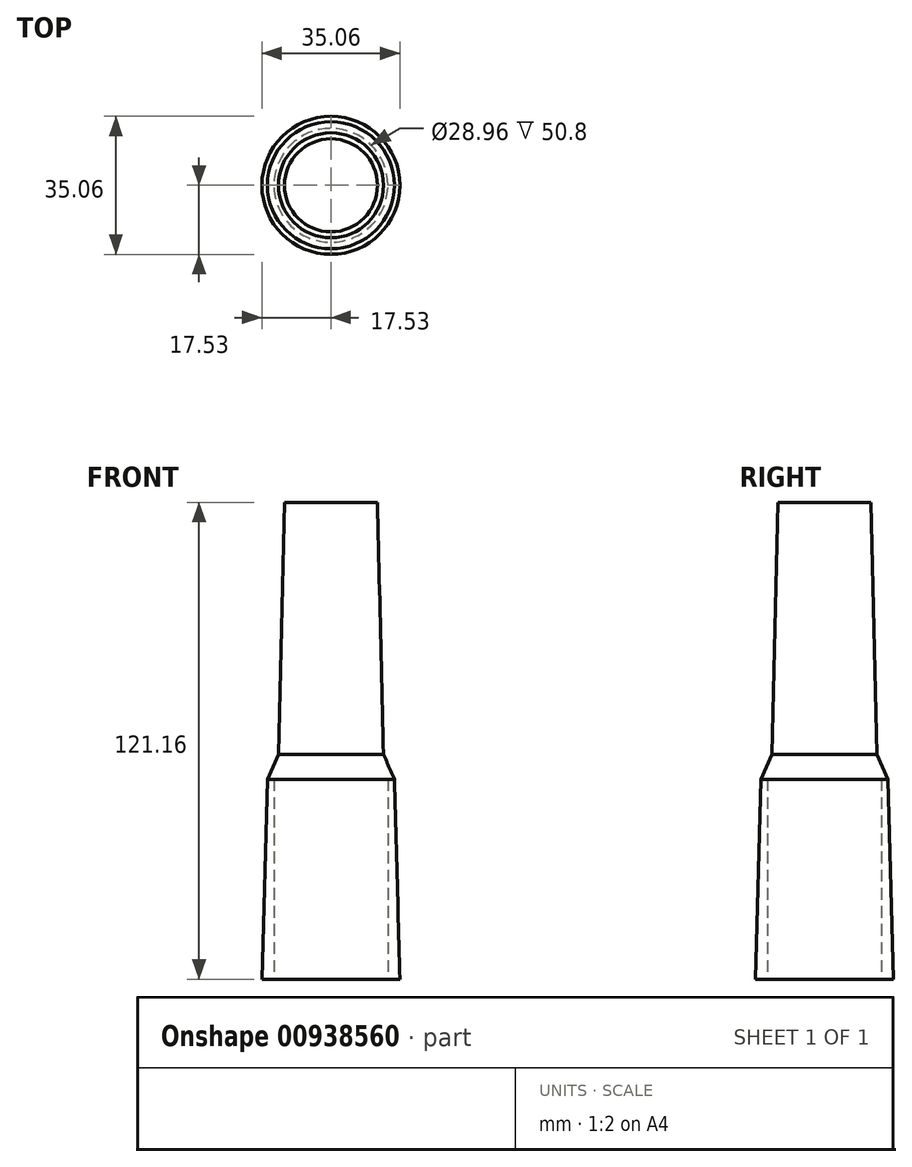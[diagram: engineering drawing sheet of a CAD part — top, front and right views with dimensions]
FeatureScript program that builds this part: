
annotation { "Feature Type Name" : "Feature", "Feature Type Description" : "" }
export const myFeature = defineFeature(function(context is Context, id is Id, definition is map)
    precondition{}
    {
        {
            var Q0;
            Q0=qCreatedBy(makeId("Top.planeOp"),FACE);
            var sketch = newSketch(context, id + "F0", { "sketchPlane" : qUnion([Q0])});
            skCircle(sketch, "E0", {"center": v(0, 0) * mm, "radius": 17.53 * mm});
            skSolve(sketch);
        }
        {
            var Q0;
            Q0=qCreatedBy(makeId("Top.planeOp"),FACE);
            cPlane(context, id + "F1", {"entities" : qUnion([Q0]), "cplaneType" : CPlaneType.OFFSET, "offset" : 50.8 * mm, "width" : 152.4 * mm, "height" : 152.4 * mm});
        }
        {
            var Q0;
            Q0=qCreatedBy(id+"F1.planeOp",FACE);
            var sketch = newSketch(context, id + "F2", { "sketchPlane" : qUnion([Q0])});
            skCircle(sketch, "E1", {"center": v(0, 0) * mm, "radius": 16.13 * mm});
            skSolve(sketch);
        }
        {
            var Q0;
            Q0=makeQuery(id+"F0.imprint","IMPRINT",FACE,{"disambiguationData":[TD([[makeQuery(id+"F0.imprint","IMPRINT",EDGE,{"derivedFrom":sQuery(id+"F0.wireOp",EDGE,"E0")}),1.0]])]});
            var Q1;
            Q1=makeQuery(id+"F2.imprint","IMPRINT",FACE,{"disambiguationData":[TD([[makeQuery(id+"F2.imprint","IMPRINT",EDGE,{"derivedFrom":sQuery(id+"F2.wireOp",EDGE,"E1")}),1.0]])]});
            loft(context, id + "F3", {"sheetProfilesArray" : [{ "sheetProfileEntities" : qUnion([Q0]) }, { "sheetProfileEntities" : qUnion([Q1]) }]});
        }
        {
            var Q0;
            Q0=qCreatedBy(id+"F1.planeOp",FACE);
            cPlane(context, id + "F4", {"entities" : qUnion([Q0]), "cplaneType" : CPlaneType.OFFSET, "offset" : 6.35 * mm, "width" : 152.4 * mm, "height" : 152.4 * mm});
        }
        {
            var Q0;
            Q0=qCreatedBy(id+"F4.planeOp",FACE);
            var sketch = newSketch(context, id + "F5", { "sketchPlane" : qUnion([Q0])});
            skCircle(sketch, "E2", {"center": v(0, 0) * mm, "radius": 13.34 * mm});
            skSolve(sketch);
        }
        {
            var Q1;
            Q1=makeQuery(id+"F3.opLoft","CAP_FACE",FACE,{"disambiguationData":[OSD([makeQuery(id+"F2.imprint","IMPRINT",FACE,{"disambiguationData":[TD([[makeQuery(id+"F2.imprint","IMPRINT",EDGE,{"derivedFrom":sQuery(id+"F2.wireOp",EDGE,"E1")}),1.0]])]})])],"isStart":true});
            var Q2;
            Q2=makeQuery(id+"F5.imprint","IMPRINT",FACE,{"disambiguationData":[TD([[makeQuery(id+"F5.imprint","IMPRINT",EDGE,{"derivedFrom":sQuery(id+"F5.wireOp",EDGE,"E2")}),1.0]])]});
            loft(context, id + "F6", {"operationType" : NewBodyOperationType.ADD, "sheetProfilesArray" : [{ "sheetProfileEntities" : qUnion([Q1]) }, { "sheetProfileEntities" : qUnion([Q2]) }]});
        }
        {
            var Q0;
            Q0=qCreatedBy(id+"F4.planeOp",FACE);
            cPlane(context, id + "F7", {"entities" : qUnion([Q0]), "cplaneType" : CPlaneType.OFFSET, "offset" : 64 * mm, "width" : 152.4 * mm, "height" : 152.4 * mm});
        }
        {
            var Q0;
            Q0=qCreatedBy(id+"F7.planeOp",FACE);
            var sketch = newSketch(context, id + "F8", { "sketchPlane" : qUnion([Q0])});
            skCircle(sketch, "E3", {"center": v(0, 0) * mm, "radius": 11.81 * mm});
            skSolve(sketch);
        }
        {
            var Q1;
            Q1=makeQuery(id+"F6.opLoft","CAP_FACE",FACE,{"disambiguationData":[OSD([makeQuery(id+"F5.imprint","IMPRINT",FACE,{"disambiguationData":[TD([[makeQuery(id+"F5.imprint","IMPRINT",EDGE,{"derivedFrom":sQuery(id+"F5.wireOp",EDGE,"E2")}),1.0]])]})])],"isStart":true});
            var Q2;
            Q2=makeQuery(id+"F8.imprint","IMPRINT",FACE,{"disambiguationData":[TD([[makeQuery(id+"F8.imprint","IMPRINT",EDGE,{"derivedFrom":sQuery(id+"F8.wireOp",EDGE,"E3")}),1.0]])]});
            loft(context, id + "F9", {"operationType" : NewBodyOperationType.ADD, "sheetProfilesArray" : [{ "sheetProfileEntities" : qUnion([Q1]) }, { "sheetProfileEntities" : qUnion([Q2]) }]});
        }
        {
            var Q0;
            Q0=makeQuery(id+"F3.opLoft","CAP_FACE",FACE,{"disambiguationData":[OSD([makeQuery(id+"F0.imprint","IMPRINT",FACE,{"disambiguationData":[TD([[makeQuery(id+"F0.imprint","IMPRINT",EDGE,{"derivedFrom":sQuery(id+"F0.wireOp",EDGE,"E0")}),1.0]])]})])],"isStart":true});
            var sketch = newSketch(context, id + "F10", { "sketchPlane" : qUnion([Q0])});
            skCircle(sketch, "E4", {"center": v(0, 0) * mm, "radius": 14.48 * mm});
            skSolve(sketch);
        }
        {
            var Q0;
            Q0 = qSketchRegion(id + "F10", true);
            extrude(context, id + "F11", {"entities" : qUnion([Q0]), "operationType" : NewBodyOperationType.REMOVE, "oppositeDirection" : true, "depth" : 50.8 * mm, "offsetDistance" : 25.4 * mm});
        }
    });
